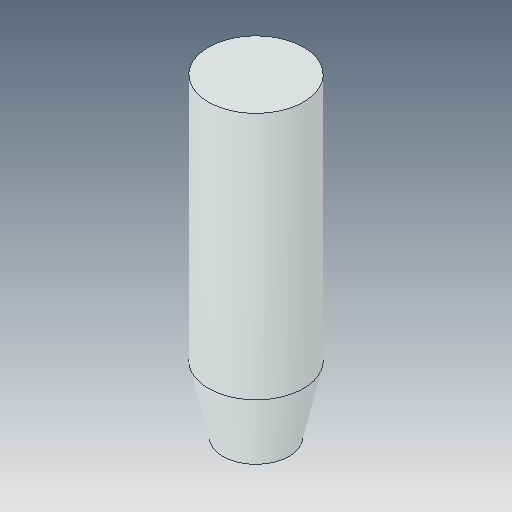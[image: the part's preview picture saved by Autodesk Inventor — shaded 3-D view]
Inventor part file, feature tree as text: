
AUTODESK INVENTOR PART (.ipt)
format: ipt  version: 2023.5 (Build 275446000, 446)  size: 87,552 bytes
history: native  units: in
note: dims shown in document units (in); Inventor stores cm internally (conversion verified against a paired STEP export)
features: chamfer x1
ambient origin geometry x8: Origin, YZ Plane, XZ Plane, XY Plane, X Axis, Y Axis, Z Axis, Center Point
bodies: Solid1 (feature_tree)
feature tree (1):
  chamfer  "Chamfer1"  [1 undecoded]
note: 1 required parameter value undecoded (feature->parameter linkage not recoverable at this tier; creation-order binding heuristic only, values carry confidence <= 0.55)
